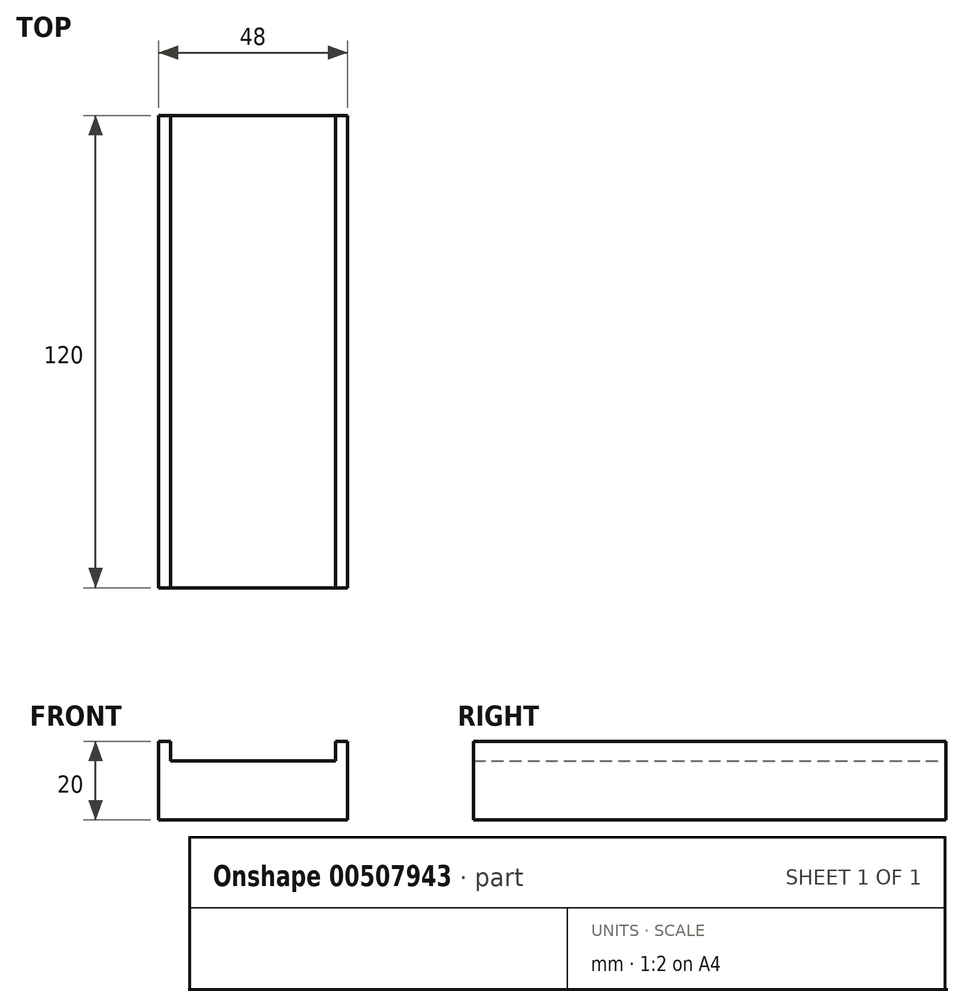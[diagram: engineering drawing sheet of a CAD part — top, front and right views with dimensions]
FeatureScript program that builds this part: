
annotation { "Feature Type Name" : "Feature", "Feature Type Description" : "" }
export const myFeature = defineFeature(function(context is Context, id is Id, definition is map)
    precondition{}
    {
        {
            var Q0;
            Q0=qCreatedBy(makeId("Front.planeOp"),FACE);
            var sketch = newSketch(context, id + "F0", { "sketchPlane" : qUnion([Q0])});
            skLineSegment(sketch, "E0", {"start": v(-38.56, 7.7) * mm, "end": v(-38.56, -12.3) * mm});
            skLineSegment(sketch, "E1", {"start": v(-38.56, -12.3) * mm, "end": v(9.44, -12.3) * mm});
            skLineSegment(sketch, "E2", {"start": v(-38.56, 7.7) * mm, "end": v(-35.56, 7.7) * mm});
            skLineSegment(sketch, "E3", {"start": v(-35.56, 7.7) * mm, "end": v(-35.56, 2.7) * mm});
            skLineSegment(sketch, "E4", {"start": v(-35.56, 2.7) * mm, "end": v(6.44, 2.7) * mm});
            skLineSegment(sketch, "E5", {"start": v(6.44, 2.7) * mm, "end": v(6.44, 7.7) * mm});
            skLineSegment(sketch, "E6", {"start": v(6.44, 7.7) * mm, "end": v(9.44, 7.7) * mm});
            skLineSegment(sketch, "E7", {"start": v(9.44, 7.7) * mm, "end": v(9.44, -12.3) * mm});
            skSolve(sketch);
        }
        {
            var Q0;
            Q0=makeQuery(id+"F0.imprint","IMPRINT",FACE,{"disambiguationData":[TD([[makeQuery(id+"F0.imprint","IMPRINT",EDGE,{"derivedFrom":sQuery(id+"F0.wireOp",EDGE,"E0")}),1.0]])]});
            extrude(context, id + "F1", {"entities" : qUnion([Q0]), "depth" : 120 * mm});
        }
    });
